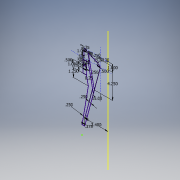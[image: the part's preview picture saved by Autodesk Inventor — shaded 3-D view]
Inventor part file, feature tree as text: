
AUTODESK INVENTOR PART (.ipt)
format: ipt  version: 2017 SP1 (Build 210196100, 196)  size: 129,024 bytes
history: native  units: in
note: dims shown in document units (in); Inventor stores cm internally (conversion verified against a paired STEP export)
features: sketch x1
ambient origin geometry x8: Origin, YZ Plane, XZ Plane, XY Plane, X Axis, Y Axis, Z Axis, Center Point
feature tree (1):
  sketch  "Sketch1"  dims[d0=1.13in d3=0.1718in d5=1.0in d6=1.0in d7=90.0deg d8=0.5in d9=15.0deg d31=0.25in d34=15.0deg d37=1.75in d40=3.75in d41=0.125in d46=0.75in d47=0.5in d51=0.5in d52=0.25in d54=0.5in d55=0.5in d56=1.25in d58=0.0017in d59=0.5in d60=0.5in d61=1.0in d62=0.234in d63=0.234in d64=0.125in d67=0.25in d68=4.25in d69=0.25in d70=0.25in d71=0.375in d73=3.4in d74=1.25in d75=0.2498in]
